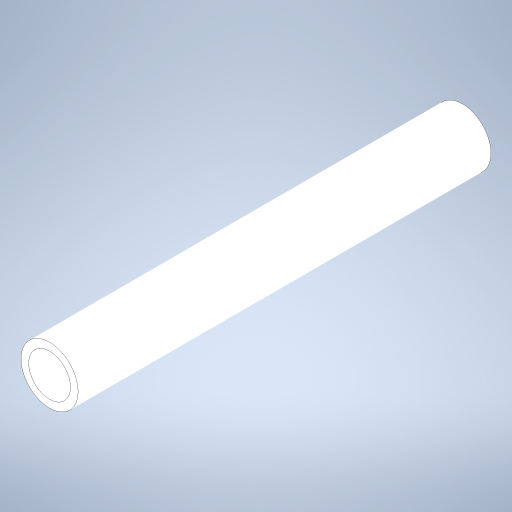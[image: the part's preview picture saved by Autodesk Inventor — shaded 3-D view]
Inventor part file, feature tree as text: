
AUTODESK INVENTOR PART (.ipt)
format: ipt  version: 2023 (Build 270158000, 158)  size: 214,016 bytes
history: native  units: mm
features: extrude x1, sketch x1
ambient origin geometry x8: Origin, YZ Plane, XZ Plane, XY Plane, X Axis, Y Axis, Z Axis, Center Point
bodies: Solid1 (feature_tree)
feature tree (2):
  extrude  "Extrusion1"  Depth=59.0mm
  sketch  "Sketch1"  dims[d0=8.15mm d1=5.96mm d2=59.0mm d3=0.0mm]
